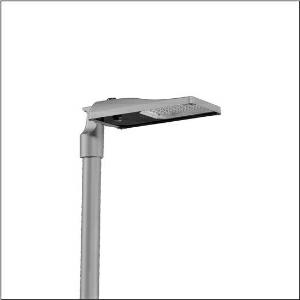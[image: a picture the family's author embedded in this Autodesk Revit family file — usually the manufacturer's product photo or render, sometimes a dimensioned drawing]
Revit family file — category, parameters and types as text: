
# Revit family: streetlight_sl_31_mini___st1_0a_5xh2d31t08ha_99ca
name_source: partatom
category: Lighting Fixtures
units: mm (PartAtom-declared; Revit-internal decimal feet)

## family parameters
Cut with Voids When Loaded = No
Host = Face
Light Source = No
Part Type = Normal
Room Calculation Point = No
Round Connector Dimension = Use Diameter
Shared = No

## types (1)
- --- (1 x LED, 9230 lm, 68.3 W, 3000K)
    Apparent Load = 68 VA
    CIE Flux Codes = 37 72 97 100 100
    Color Rendering = 70
    Color Temperature = 3000K
    Default Elevation = 1800 mm
    Description = Streetlight SL 31 mini D4i, Desk-Remote mast luminaire for post-top, side-entry; light control with lens of PMMA; light distribution: ST1.0a, direct asymmetric distribution, for standard-compliant lighting for roads and squares; LED: luminous flux: 9.230lm, light colour: 730, colour temperature: 3000K; luminous efficacy: 135,1lm/W; control: pre-setting: logarithmic dimming characteristic, flexible luminous flux parameterisation, time-dependent luminous flux control, constant luminous flux control, power reduction, intelligent temperature release in ECG and LED module, overheat protection; luminaire housing, of diecast aluminium, SITECO metallic grey (DB 702S), corrosivity category C5 high according to DIN EN ISO 12944; cover of toughened safety glass, transparent, mast flange of diecast aluminium, SITECO metallic grey (DB 702S), spigot size: 76/60mm, mast flange included unmounted; with cable H07RN-F 2x 1.5mm², cable length: 8,5m, connection cable pre-assembled; mains connection: 220..240V, AC, 50/60Hz; power consumption (at start of service life): 68,3W / (at end of service life): 74,5W / (with reduced operation 50%): 29,5W; protection rating (complete): IP66; insulation class (complete): insulation class II (safety insulation); impact resistance: IK09; certification: CE, ENEC, ENEC+, VDE, UKCA, ZD4i; permissible operating ambient temperature for outdoor applications: -40..+50°C; packaging unit: 1 piece

Light Distribution: ST1.0a
    Height = 76 mm
    Lamp = 1 x LED
    Lamp Light Flux = 9230 lm
    Lamp Power = 68.3 W
    Lamp count = 1
    Length = 547 mm
    Luminous efficacy = 135 lm/W
    Manufacturer = Siteco
    ModVariant = No
    Model = 5XH2D31T08HA
    Number of Poles = 1
    OnlyDefault = Yes
    Power Factor = 1
    Product Name = Streetlight SL 31 mini | ST1.0a
    Product group = mast luminaire | pylon top
    ProductGroupID = 6100
    Protection Class = Protection class II
    Protection Degree = IP 66
    RLX_Detail_Level = 1
    RLX_Emergency_Light_Flux = 0 lm
    RLX_Emergency_Type = 0
    RLX_Emergency_Type_DB = No
    RlxData = <blob elided: 39509 chars, md5=70e39b49>
    Socket = socket
    Standby Power = 0 W
    System Light Flux = 9230 lm
    System Power = 68 W
    Type Comments = factory setting: luminous flux: 100 % | dim-lin: 254 | 692 mA
    Type Image = l_1300332.jpg
    URL = http://relux.com
    VarID = @adj_020587
    Voltage = 0 V
    Weight = 0.00 kg
    Width = 265 mm

## geometry (parser evidence)
native form markers: Blend x4, Sweep x10
no freeform markers — native parametric forms only
